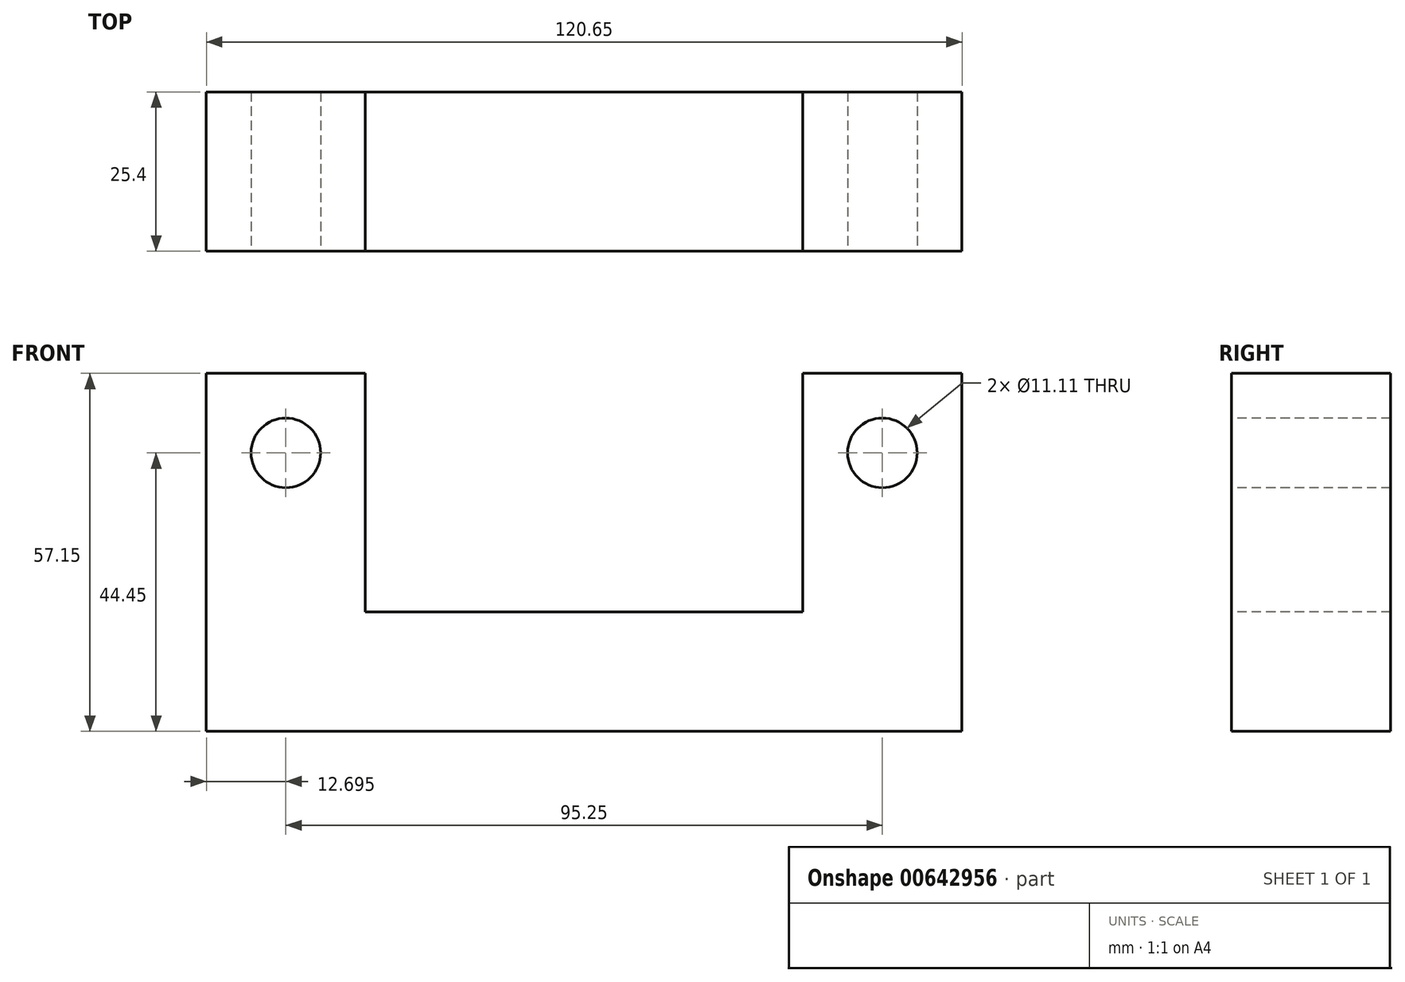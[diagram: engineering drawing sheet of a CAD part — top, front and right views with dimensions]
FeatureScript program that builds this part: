
annotation { "Feature Type Name" : "Feature", "Feature Type Description" : "" }
export const myFeature = defineFeature(function(context is Context, id is Id, definition is map)
    precondition{}
    {
        {
            var Q0;
            Q0=qCreatedBy(makeId("Top.planeOp"),FACE);
            var sketch = newSketch(context, id + "F0", { "sketchPlane" : qUnion([Q0])});
            skLineSegment(sketch, "E0.bottom", {"start": v(-52.36, -9.16) * mm, "end": v(68.29, -9.16) * mm});
            skLineSegment(sketch, "E0.top", {"start": v(-52.36, -34.56) * mm, "end": v(68.29, -34.56) * mm});
            skLineSegment(sketch, "E0.left", {"start": v(-52.36, -9.16) * mm, "end": v(-52.36, -34.56) * mm});
            skLineSegment(sketch, "E0.right", {"start": v(68.29, -9.16) * mm, "end": v(68.29, -34.56) * mm});
            skLineSegment(sketch, "E1.bottom", {"start": v(-14.26, -34.56) * mm, "end": v(30.19, -34.56) * mm});
            skLineSegment(sketch, "E1.top", {"start": v(-14.26, -66.3) * mm, "end": v(30.19, -66.3) * mm});
            skLineSegment(sketch, "E1.left", {"start": v(-14.26, -34.56) * mm, "end": v(-14.26, -66.3) * mm});
            skLineSegment(sketch, "E1.right", {"start": v(30.19, -34.56) * mm, "end": v(30.19, -66.3) * mm});
            skSolve(sketch);
        }
        {
            var Q0;
            Q0=makeQuery(id+"F0.imprint","IMPRINT",FACE,{"disambiguationData":[TD([[makeQuery(id+"F0.imprint","IMPRINT",EDGE,{"derivedFrom":sQuery(id+"F0.wireOp",EDGE,"E0.bottom")}),-1.0]])]});
            var Q1;
            Q1=makeQuery(id+"F0.imprint","IMPRINT",FACE,{"disambiguationData":[TD([[makeQuery(id+"F0.imprint","IMPRINT",EDGE,{"derivedFrom":sQuery(id+"F0.wireOp",EDGE,"E1.bottom")}),-1.0]])]});
            extrude(context, id + "F1", {"entities" : qUnion([Q0, Q1]), "depth" : 19.05 * mm, "offsetDistance" : 25.4 * mm});
        }
        {
            var Q0;
            Q0=makeQuery(id+"F1.opExtrude","CAP_FACE",FACE,{"disambiguationData":[OSD([sQuery(id+"F0.wireOp",EDGE,"E0.bottom"),sQuery(id+"F0.wireOp",EDGE,"E0.top"),sQuery(id+"F0.wireOp",EDGE,"E0.left"),sQuery(id+"F0.wireOp",EDGE,"E0.right"),sQuery(id+"F0.wireOp",EDGE,"E1.top"),sQuery(id+"F0.wireOp",EDGE,"E1.left"),sQuery(id+"F0.wireOp",EDGE,"E1.right")])],"isStart":false});
            var sketch = newSketch(context, id + "F2", { "sketchPlane" : qUnion([Q0])});
            skCircle(sketch, "E2", {"center": v(7.96, -50.43) * mm, "radius": 7.94 * mm});
            skPoint(sketch, "E2.centerSnap0", {"position": v(7.96, -66.3) * mm});
            skSolve(sketch);
        }
        {
            var Q0;
            Q0=makeQuery(id+"F2.imprint","IMPRINT",FACE,{"disambiguationData":[TD([[makeQuery(id+"F2.imprint","IMPRINT",EDGE,{"derivedFrom":sQuery(id+"F2.wireOp",EDGE,"E2")}),1.0]])]});
            extrude(context, id + "F3", {"entities" : qUnion([Q0]), "operationType" : NewBodyOperationType.REMOVE, "endBound" : BoundingType.THROUGH_ALL, "oppositeDirection" : true, "depth" : 25.4 * mm, "offsetDistance" : 25.4 * mm});
        }
        {
            var Q0;
            Q0=makeQuery(id+"F1.opExtrude","CAP_FACE",FACE,{"disambiguationData":[OSD([sQuery(id+"F0.wireOp",EDGE,"E0.bottom"),sQuery(id+"F0.wireOp",EDGE,"E0.top"),sQuery(id+"F0.wireOp",EDGE,"E0.left"),sQuery(id+"F0.wireOp",EDGE,"E0.right"),sQuery(id+"F0.wireOp",EDGE,"E1.top"),sQuery(id+"F0.wireOp",EDGE,"E1.left"),sQuery(id+"F0.wireOp",EDGE,"E1.right")])],"isStart":false});
            var sketch = newSketch(context, id + "F4", { "sketchPlane" : qUnion([Q0])});
            skLineSegment(sketch, "E3.bottom", {"start": v(-52.36, -9.16) * mm, "end": v(-26.96, -9.16) * mm});
            skLineSegment(sketch, "E3.top", {"start": v(-52.36, -34.56) * mm, "end": v(-26.96, -34.56) * mm});
            skLineSegment(sketch, "E3.left", {"start": v(-52.36, -9.16) * mm, "end": v(-52.36, -34.56) * mm});
            skLineSegment(sketch, "E3.right", {"start": v(-26.96, -9.16) * mm, "end": v(-26.96, -34.56) * mm});
            skLineSegment(sketch, "E4.bottom", {"start": v(68.29, -9.16) * mm, "end": v(42.89, -9.16) * mm});
            skLineSegment(sketch, "E4.top", {"start": v(68.29, -34.56) * mm, "end": v(42.89, -34.56) * mm});
            skLineSegment(sketch, "E4.left", {"start": v(68.29, -9.16) * mm, "end": v(68.29, -34.56) * mm});
            skLineSegment(sketch, "E4.right", {"start": v(42.89, -9.16) * mm, "end": v(42.89, -34.56) * mm});
            skSolve(sketch);
        }
        {
            var Q0;
            Q0=makeQuery(id+"F4.imprint","IMPRINT",FACE,{"disambiguationData":[TD([[makeQuery(id+"F4.imprint","IMPRINT",EDGE,{"derivedFrom":sQuery(id+"F4.wireOp",EDGE,"E3.bottom")}),-1.0]])]});
            var Q1;
            Q1=makeQuery(id+"F4.imprint","IMPRINT",FACE,{"disambiguationData":[TD([[makeQuery(id+"F4.imprint","IMPRINT",EDGE,{"derivedFrom":sQuery(id+"F4.wireOp",EDGE,"E4.bottom")}),-1.0]])]});
            extrude(context, id + "F5", {"entities" : qUnion([Q0, Q1]), "operationType" : NewBodyOperationType.ADD, "depth" : 38.1 * mm, "offsetDistance" : 25.4 * mm});
        }
        {
            var Q0;
            {var subQ0=sQuery(id+"F0.wireOp",EDGE,"E0.top");Q0=makeQuery(id+"F5.boolean.opBoolean","MERGE",FACE,{"derivedFrom":[makeQuery(id+"F1.opExtrude","SWEPT_FACE",FACE,{"disambiguationData":[OSD([subQ0]),TDD([makeQuery(id+"F0.imprint","IMPRINT",EDGE,{"disambiguationData":[TD([[makeQuery(id+"F0.imprint","INTERSECT",VERTEX,{"derivedFrom":[subQ0,sQuery(id+"F0.wireOp",EDGE,"E0.left")]}),-1.0]])],"derivedFrom":subQ0})])]}),makeQuery(id+"F5.opExtrude","SWEPT_FACE",FACE,{"disambiguationData":[OSD([sQuery(id+"F4.wireOp",EDGE,"E3.top")])]})]});}
            var sketch = newSketch(context, id + "F6", { "sketchPlane" : qUnion([Q0])});
            skCircle(sketch, "E5", {"center": v(-39.66, 44.45) * mm, "radius": 5.56 * mm});
            skPoint(sketch, "E5.centerSnap0", {"position": v(-39.66, 57.15) * mm});
            skSolve(sketch);
        }
        {
            var Q0;
            Q0=makeQuery(id+"F6.imprint","IMPRINT",FACE,{"disambiguationData":[TD([[makeQuery(id+"F6.imprint","IMPRINT",EDGE,{"derivedFrom":sQuery(id+"F6.wireOp",EDGE,"E5")}),1.0]])]});
            extrude(context, id + "F7", {"entities" : qUnion([Q0]), "operationType" : NewBodyOperationType.REMOVE, "endBound" : BoundingType.THROUGH_ALL, "oppositeDirection" : true, "depth" : 25.4 * mm, "offsetDistance" : 25.4 * mm});
        }
        {
            var Q0;
            {var subQ0=sQuery(id+"F0.wireOp",EDGE,"E0.top");Q0=makeQuery(id+"F5.boolean.opBoolean","MERGE",FACE,{"derivedFrom":[makeQuery(id+"F1.opExtrude","SWEPT_FACE",FACE,{"disambiguationData":[OSD([subQ0]),TDD([makeQuery(id+"F0.imprint","IMPRINT",EDGE,{"disambiguationData":[TD([[makeQuery(id+"F0.imprint","INTERSECT",VERTEX,{"derivedFrom":[subQ0,sQuery(id+"F0.wireOp",EDGE,"E0.right")]}),1.0]])],"derivedFrom":subQ0})])]}),makeQuery(id+"F5.opExtrude","SWEPT_FACE",FACE,{"disambiguationData":[OSD([sQuery(id+"F4.wireOp",EDGE,"E4.top")])]})]});}
            var sketch = newSketch(context, id + "F8", { "sketchPlane" : qUnion([Q0])});
            skCircle(sketch, "E6", {"center": v(55.59, 44.45) * mm, "radius": 5.56 * mm});
            skPoint(sketch, "E6.centerSnap0", {"position": v(55.59, 57.15) * mm});
            skSolve(sketch);
        }
        {
            var Q0;
            Q0=makeQuery(id+"F8.imprint","IMPRINT",FACE,{"disambiguationData":[TD([[makeQuery(id+"F8.imprint","IMPRINT",EDGE,{"derivedFrom":sQuery(id+"F8.wireOp",EDGE,"E6")}),1.0]])]});
            extrude(context, id + "F9", {"entities" : qUnion([Q0]), "operationType" : NewBodyOperationType.REMOVE, "endBound" : BoundingType.THROUGH_ALL, "oppositeDirection" : true, "depth" : 25.4 * mm, "offsetDistance" : 25.4 * mm});
        }
    });
